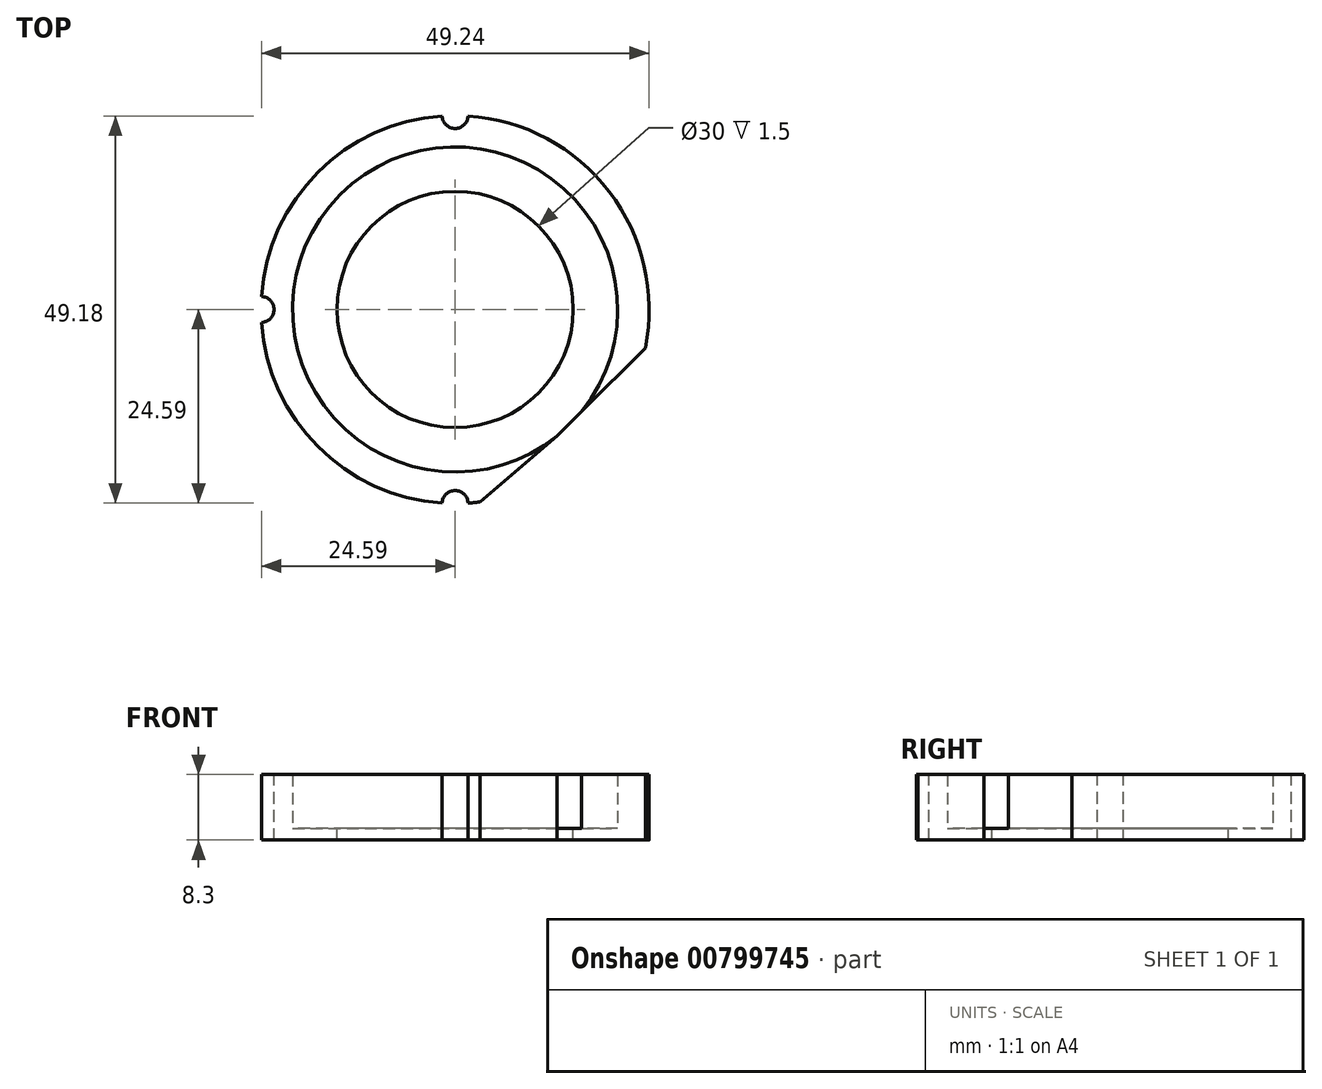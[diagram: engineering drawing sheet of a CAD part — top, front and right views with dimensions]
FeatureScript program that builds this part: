
annotation { "Feature Type Name" : "Feature", "Feature Type Description" : "" }
export const myFeature = defineFeature(function(context is Context, id is Id, definition is map)
    precondition{}
    {
        {
            var Q0;
            Q0=qCreatedBy(makeId("Top.planeOp"),FACE);
            var sketch = newSketch(context, id + "F0", { "sketchPlane" : qUnion([Q0])});
            skCircle(sketch, "E0", {"center": v(0, 0) * mm, "radius": 15 * mm});
            skCircle(sketch, "E1", {"center": v(0, 0) * mm, "radius": 24.65 * mm});
            skCircle(sketch, "E2", {"center": v(0, 0) * mm, "radius": 27.8 * mm});
            skCircle(sketch, "E3", {"center": v(0, 0) * mm, "radius": 20.65 * mm});
            skPoint(sketch, "E4", {"position": v(0, 24.65) * mm});
            skPoint(sketch, "E5", {"position": v(-24.65, 0) * mm});
            skPoint(sketch, "E6", {"position": v(0, -24.65) * mm});
            skCircle(sketch, "E7", {"center": v(0, 24.65) * mm, "radius": 1.65 * mm});
            skCircle(sketch, "E8", {"center": v(-24.65, 0) * mm, "radius": 1.65 * mm});
            skCircle(sketch, "E9", {"center": v(0, -24.65) * mm, "radius": 1.65 * mm});
            skPoint(sketch, "E10", {"position": v(0, 27.8) * mm});
            skPoint(sketch, "E11", {"position": v(29.24, 27.8) * mm});
            skPoint(sketch, "E12", {"position": v(19.65, 0) * mm});
            skPoint(sketch, "E13", {"position": v(19.65, 19.67) * mm});
            skLineSegment(sketch, "E14", {"start": v(19.65, 19.67) * mm, "end": v(41.79, -2.45) * mm});
            skPoint(sketch, "E15", {"position": v(12.97, -16.07) * mm});
            skLineSegment(sketch, "E16", {"start": v(12.97, -16.07) * mm, "end": v(34.17, 5.15) * mm});
            skCircle(sketch, "E17", {"center": v(0, -24.65) * mm, "radius": 3.15 * mm});
            skLineSegment(sketch, "E18", {"start": v(12.97, -16.07) * mm, "end": v(3.14, -24.45) * mm});
            skSolve(sketch);
        }
        {
            var Q0;
            Q0=makeQuery(id+"F0.imprint","IMPRINT",FACE,{"disambiguationData":[TD([[makeQuery(id+"F0.imprint","IMPRINT",EDGE,{"derivedFrom":sQuery(id+"F0.wireOp",EDGE,"E0")}),-1.0]])]});
            var Q1;
            {var subQ6=sQuery(id+"F0.wireOp",EDGE,"E7");var subQ17=makeQuery(id+"F0.imprint","IMPRINT",VERTEX,{"derivedFrom":subQ6});Q1=makeQuery(id+"F0.imprint","IMPRINT",FACE,{"disambiguationData":[TD([[makeQuery(id+"F0.imprint","IMPRINT",EDGE,{"disambiguationData":[TD([[subQ17,-1.0]])],"derivedFrom":subQ6}),-1.0]])]});}
            var Q2;
            {var subQ1=sQuery(id+"F0.wireOp",EDGE,"E2");var subQ3=makeQuery(id+"F0.imprint","IMPRINT",VERTEX,{"derivedFrom":subQ1});Q2=makeQuery(id+"F0.imprint","IMPRINT",FACE,{"disambiguationData":[TD([[makeQuery(id+"F0.imprint","IMPRINT",EDGE,{"disambiguationData":[TD([[subQ3,1.0]])],"derivedFrom":subQ1}),-1.0]])]});}
            var Q3;
            {var subQ4=sQuery(id+"F0.wireOp",EDGE,"E1");var subQ5=makeQuery(id+"F0.imprint","IMPRINT",VERTEX,{"derivedFrom":subQ4});Q3=makeQuery(id+"F0.imprint","IMPRINT",FACE,{"disambiguationData":[TD([[makeQuery(id+"F0.imprint","IMPRINT",EDGE,{"disambiguationData":[TD([[subQ5,-1.0]])],"derivedFrom":subQ4}),-1.0]])]});}
            var Q4;
            {var subQ0=sQuery(id+"F0.wireOp",EDGE,"E17");var subQ1=sQuery(id+"F0.wireOp",EDGE,"E1");var subQ2=makeQuery(id+"F0.imprint","INTERSECT",VERTEX,{"derivedFrom":[subQ1,subQ0]});Q4=makeQuery(id+"F0.imprint","IMPRINT",FACE,{"disambiguationData":[TD([[makeQuery(id+"F0.imprint","IMPRINT",EDGE,{"disambiguationData":[TD([[subQ2,-1.0]])],"derivedFrom":subQ1}),1.0]])]});}
            var Q5;
            {var subQ0=sQuery(id+"F0.wireOp",EDGE,"E9");var subQ1=makeQuery(id+"F0.imprint","IMPRINT",VERTEX,{"derivedFrom":subQ0});Q5=makeQuery(id+"F0.imprint","IMPRINT",FACE,{"disambiguationData":[TD([[makeQuery(id+"F0.imprint","IMPRINT",EDGE,{"disambiguationData":[TD([[subQ1,-1.0]])],"derivedFrom":subQ0}),-1.0]])]});}
            var Q6;
            {var subQ13=sQuery(id+"F0.wireOp",EDGE,"E18");Q6=makeQuery(id+"F0.imprint","IMPRINT",FACE,{"disambiguationData":[TD([[makeQuery(id+"F0.imprint","IMPRINT",EDGE,{"derivedFrom":subQ13}),-1.0]])]});}
            extrude(context, id + "F1", {"entities" : qUnion([Q0, Q1, Q2, Q3, Q4, Q5, Q6]), "oppositeDirection" : true, "depth" : 1.5 * mm, "offsetDistance" : 25 * mm});
        }
        {
            var Q0;
            {var subQ13=sQuery(id+"F0.wireOp",EDGE,"E18");Q0=makeQuery(id+"F0.imprint","IMPRINT",FACE,{"disambiguationData":[TD([[makeQuery(id+"F0.imprint","IMPRINT",EDGE,{"derivedFrom":subQ13}),-1.0]])]});}
            var Q1;
            {var subQ2=sQuery(id+"F0.wireOp",EDGE,"E1");var subQ14=makeQuery(id+"F0.imprint","IMPRINT",VERTEX,{"derivedFrom":subQ2});Q1=makeQuery(id+"F0.imprint","IMPRINT",FACE,{"disambiguationData":[TD([[makeQuery(id+"F0.imprint","IMPRINT",EDGE,{"disambiguationData":[TD([[subQ14,-1.0]])],"derivedFrom":subQ2}),-1.0]])]});}
            var Q2;
            {var subQ1=sQuery(id+"F0.wireOp",EDGE,"E2");var subQ3=makeQuery(id+"F0.imprint","IMPRINT",VERTEX,{"derivedFrom":subQ1});Q2=makeQuery(id+"F0.imprint","IMPRINT",FACE,{"disambiguationData":[TD([[makeQuery(id+"F0.imprint","IMPRINT",EDGE,{"disambiguationData":[TD([[subQ3,-1.0]])],"derivedFrom":subQ1}),-1.0]])]});}
            var Q3;
            {var subQ0=sQuery(id+"F0.wireOp",EDGE,"E9");var subQ1=makeQuery(id+"F0.imprint","IMPRINT",VERTEX,{"derivedFrom":subQ0});Q3=makeQuery(id+"F0.imprint","IMPRINT",FACE,{"disambiguationData":[TD([[makeQuery(id+"F0.imprint","IMPRINT",EDGE,{"disambiguationData":[TD([[subQ1,-1.0]])],"derivedFrom":subQ0}),-1.0]])]});}
            var Q4;
            {var subQ0=sQuery(id+"F0.wireOp",EDGE,"E17");var subQ1=sQuery(id+"F0.wireOp",EDGE,"E1");var subQ2=makeQuery(id+"F0.imprint","INTERSECT",VERTEX,{"derivedFrom":[subQ1,subQ0]});Q4=makeQuery(id+"F0.imprint","IMPRINT",FACE,{"disambiguationData":[TD([[makeQuery(id+"F0.imprint","IMPRINT",EDGE,{"disambiguationData":[TD([[subQ2,-1.0]])],"derivedFrom":subQ1}),1.0]])]});}
            extrude(context, id + "F2", {"entities" : qUnion([Q0, Q1, Q2, Q3, Q4]), "operationType" : NewBodyOperationType.ADD, "depth" : 6.8 * mm, "offsetDistance" : 25 * mm});
        }
    });
